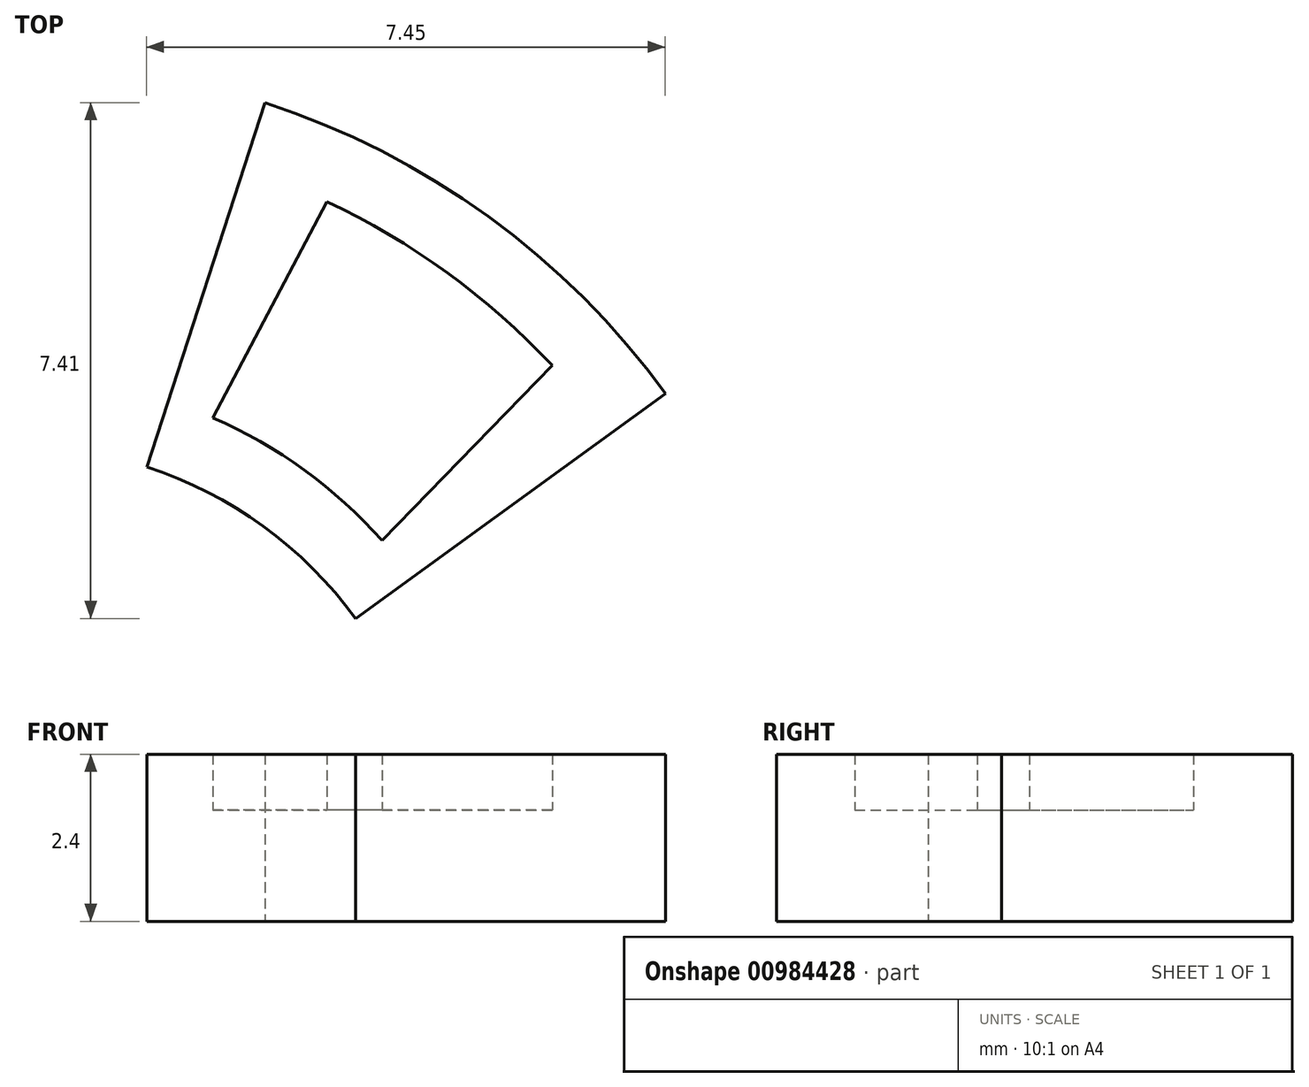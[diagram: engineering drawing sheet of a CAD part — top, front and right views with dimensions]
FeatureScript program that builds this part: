
annotation { "Feature Type Name" : "Feature", "Feature Type Description" : "" }
export const myFeature = defineFeature(function(context is Context, id is Id, definition is map)
    precondition{}
    {
        {
            var Q0;
            Q0=qCreatedBy(makeId("Top.planeOp"),FACE);
            var sketch = newSketch(context, id + "F0", { "sketchPlane" : qUnion([Q0])});
            skArc(sketch, "E0.9.0", {"start": v(2.8, 6.41) * mm, "mid": v(4.11, 5.66) * mm, "end": v(5.23, 4.65) * mm});
            skArc(sketch, "E0.9.1", {"start": v(4.44, 9.51) * mm, "mid": v(6.17, 8.5) * mm, "end": v(7.68, 7.16) * mm});
            skLineSegment(sketch, "E0.9.2", {"start": v(5.23, 4.65) * mm, "end": v(7.68, 7.16) * mm});
            skLineSegment(sketch, "E0.9.3", {"start": v(2.8, 6.41) * mm, "end": v(4.44, 9.51) * mm});
            skLineSegment(sketch, "E1", {"start": v(0, 0) * mm, "end": v(3.86, 11.89) * mm, "construction": true});
            skLineSegment(sketch, "E2", {"start": v(0, 0) * mm, "end": v(2.8, 6.41) * mm, "construction": true});
            skLineSegment(sketch, "E3", {"start": v(0, 0) * mm, "end": v(10.11, 7.35) * mm, "construction": true});
            skLineSegment(sketch, "E4", {"start": v(0, 0) * mm, "end": v(5.23, 4.65) * mm, "construction": true});
            skLineSegment(sketch, "E5", {"start": v(0, 0) * mm, "end": v(6.04, 3.54) * mm, "construction": true});
            skArc(sketch, "E6", {"start": v(1.85, 5.7) * mm, "mid": v(3.53, 4.85) * mm, "end": v(4.85, 3.53) * mm});
            skArc(sketch, "E7", {"start": v(3.55, 10.94) * mm, "mid": v(6.76, 9.3) * mm, "end": v(9.3, 6.76) * mm});
            skLineSegment(sketch, "E8", {"start": v(3.55, 10.94) * mm, "end": v(1.85, 5.7) * mm});
            skLineSegment(sketch, "E9", {"start": v(4.85, 3.53) * mm, "end": v(9.3, 6.76) * mm});
            skSolve(sketch);
        }
        {
            var Q0;
            Q0=makeQuery(id+"F0.imprint","IMPRINT",FACE,{"disambiguationData":[TD([[makeQuery(id+"F0.imprint","IMPRINT",EDGE,{"derivedFrom":sQuery(id+"F0.wireOp",EDGE,"E0.9.0")}),1.0]])]});
            extrude(context, id + "F1", {"entities" : qUnion([Q0]), "depth" : 0.8 * mm, "offsetDistance" : 25 * mm});
        }
        {
            var Q0;
            Q0=makeQuery(id+"F0.imprint","IMPRINT",FACE,{"disambiguationData":[TD([[makeQuery(id+"F0.imprint","IMPRINT",EDGE,{"derivedFrom":sQuery(id+"F0.wireOp",EDGE,"E0.9.0")}),-1.0]])]});
            var Q1;
            Q1=makeQuery(id+"F0.imprint","IMPRINT",FACE,{"disambiguationData":[TD([[makeQuery(id+"F0.imprint","IMPRINT",EDGE,{"derivedFrom":sQuery(id+"F0.wireOp",EDGE,"E0.9.0")}),1.0]])]});
            extrude(context, id + "F2", {"entities" : qUnion([Q0, Q1]), "operationType" : NewBodyOperationType.ADD, "oppositeDirection" : true, "depth" : 1.6 * mm, "offsetDistance" : 25 * mm});
        }
    });
